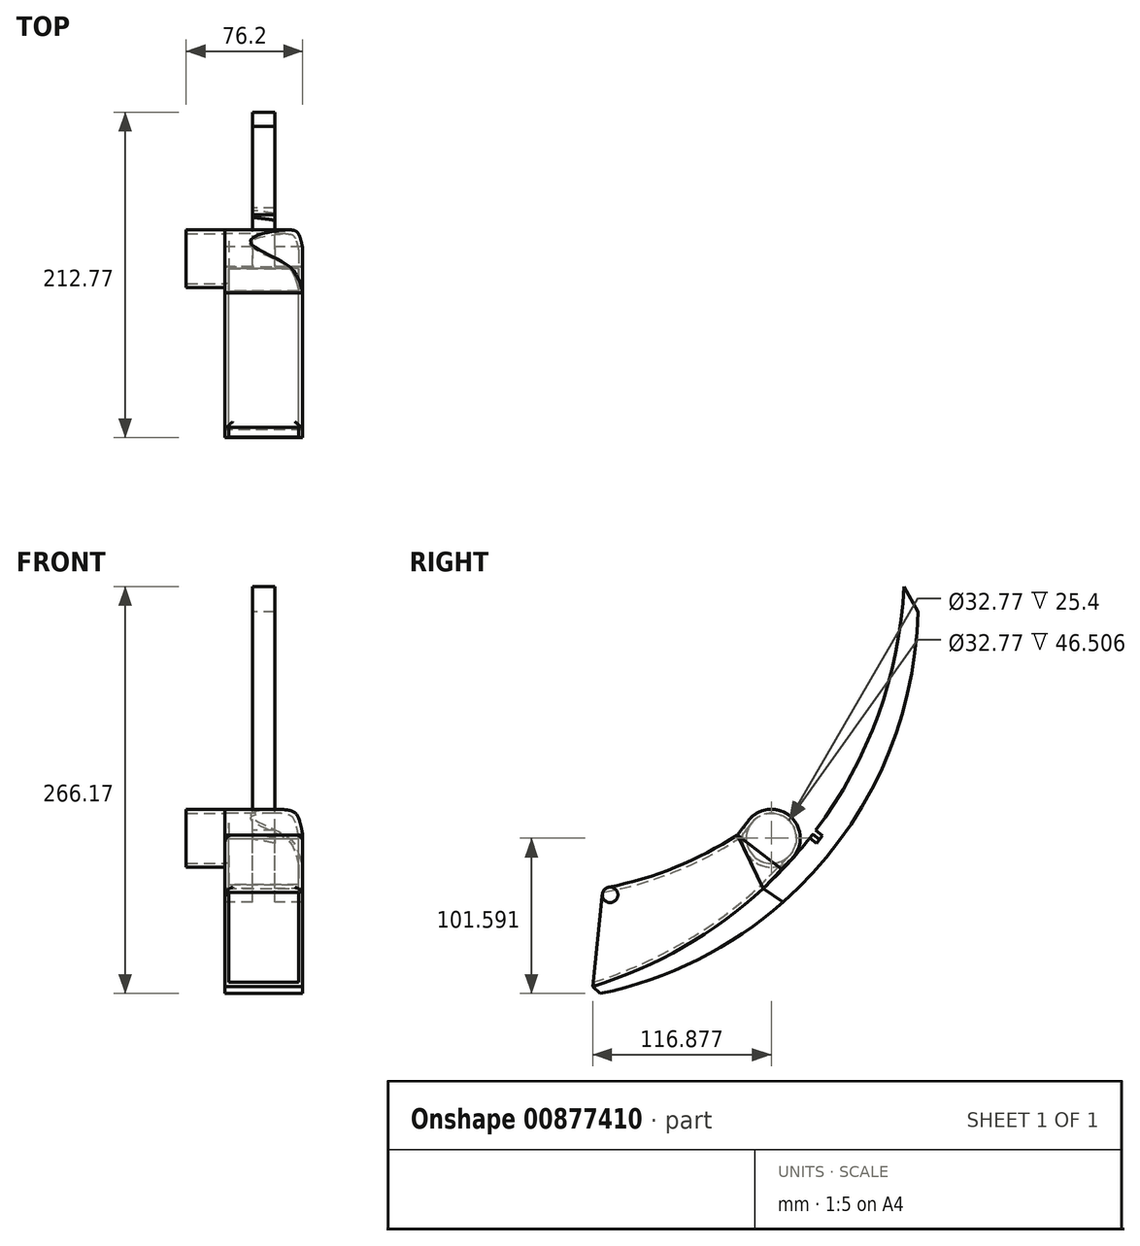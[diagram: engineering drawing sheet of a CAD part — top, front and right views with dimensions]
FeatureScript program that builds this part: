
annotation { "Feature Type Name" : "Feature", "Feature Type Description" : "" }
export const myFeature = defineFeature(function(context is Context, id is Id, definition is map)
    precondition{}
    {
        {
            var Q0;
            Q0=qCreatedBy(makeId("Right.planeOp"),FACE);
            var sketch = newSketch(context, id + "F0", { "sketchPlane" : qUnion([Q0])});
            skLineSegment(sketch, "E0", {"start": v(0, 254) * mm, "end": v(-9.14, 270.4) * mm});
            skLineSegment(sketch, "E1", {"start": v(-212.77, 8.9) * mm, "end": v(-207.84, 4.23) * mm});
            skArc(sketch, "E2", {"start": v(-207.84, 4.23) * mm, "mid": v(-60.3, 92.82) * mm, "end": v(0, 254) * mm});
            skArc(sketch, "E3", {"start": v(-212.77, 8.9) * mm, "mid": v(-69.6, 107.45) * mm, "end": v(-9.14, 270.4) * mm});
            skLineSegment(sketch, "E4", {"start": v(-88.1, 64.18) * mm, "end": v(-101.15, 73.07) * mm});
            skSolve(sketch);
        }
        {
            var Q0;
            Q0=makeQuery(id+"F0.imprint","IMPRINT",FACE,{"disambiguationData":[TD([[makeQuery(id+"F0.imprint","IMPRINT",EDGE,{"derivedFrom":sQuery(id+"F0.wireOp",EDGE,"E0")}),1.0]])]});
            extrude(context, id + "F1", {"entities" : qUnion([Q0]), "endBound" : BoundingType.SYMMETRIC, "depth" : 14.6 * mm, "offsetDistance" : 25.4 * mm});
        }
        {
            var Q0;
            {var subQ0=sQuery(id+"F0.wireOp",EDGE,"E1");Q0=makeQuery(id+"F0.imprint","IMPRINT",FACE,{"disambiguationData":[TD([[makeQuery(id+"F0.imprint","IMPRINT",EDGE,{"derivedFrom":subQ0}),1.0]])]});}
            extrude(context, id + "F2", {"entities" : qUnion([Q0]), "operationType" : NewBodyOperationType.ADD, "endBound" : BoundingType.SYMMETRIC, "depth" : 50.8 * mm, "offsetDistance" : 25.4 * mm});
        }
        {
            var Q0;
            Q0=makeQuery(id+"F2.opExtrude","CAP_FACE",FACE,{"disambiguationData":[OSD([sQuery(id+"F0.wireOp",EDGE,"E1"),sQuery(id+"F0.wireOp",EDGE,"E2"),sQuery(id+"F0.wireOp",EDGE,"E3"),sQuery(id+"F0.wireOp",EDGE,"E4")])],"isStart":false});
            var sketch = newSketch(context, id + "F3", { "sketchPlane" : qUnion([Q0])});
            skLineSegment(sketch, "E5", {"start": v(-101.15, 73.07) * mm, "end": v(-118.1, 107.95) * mm});
            skLineSegment(sketch, "E6", {"start": v(-212.77, 8.9) * mm, "end": v(-206.02, 73.07) * mm});
            skArc(sketch, "E7", {"start": v(-206.02, 73.07) * mm, "mid": v(-160.33, 86.16) * mm, "end": v(-118.1, 107.95) * mm});
            skSolve(sketch);
        }
        {
            var Q0;
            Q0=makeQuery(id+"F3.imprint","IMPRINT",FACE,{"disambiguationData":[TD([[makeQuery(id+"F3.imprint","IMPRINT",EDGE,{"derivedFrom":sQuery(id+"F3.wireOp",EDGE,"E5")}),1.0]])]});
            extrude(context, id + "F4", {"entities" : qUnion([Q0]), "oppositeDirection" : true, "depth" : 50.8 * mm, "offsetDistance" : 25.4 * mm});
        }
        {
            var Q0;
            Q0=makeQuery(id+"F4.opExtrude","SWEPT_FACE",FACE,{"disambiguationData":[OSD([sQuery(id+"F3.wireOp",EDGE,"E6")])]});
            var Q1;
            Q1=makeQuery(id+"F4.opExtrude","SWEPT_FACE",FACE,{"disambiguationData":[OSD([sQuery(id+"F3.wireOp",EDGE,"E5")])]});
            shell(context, id + "F5", {"entities" : qUnion([Q0, Q1]), "thickness" : 2.54 * mm});
        }
        {
            var Q0;
            Q0=makeQuery(id+"F4.opExtrude","CAP_FACE",FACE,{"disambiguationData":[OSD([sQuery(id+"F0.wireOp",EDGE,"E3"),sQuery(id+"F3.wireOp",EDGE,"E5"),sQuery(id+"F3.wireOp",EDGE,"E6"),sQuery(id+"F3.wireOp",EDGE,"E7")])],"isStart":false});
            var sketch = newSketch(context, id + "F6", { "sketchPlane" : qUnion([Q0])});
            skCircle(sketch, "E8", {"center": v(95.9, 105.82) * mm, "radius": 18.92 * mm});
            skLineSegment(sketch, "E9", {"start": v(82.26, 92.7) * mm, "end": v(101.15, 73.07) * mm});
            skLineSegment(sketch, "E10", {"start": v(110.92, 117.32) * mm, "end": v(118.1, 107.95) * mm});
            skSolve(sketch);
        }
        {
            var Q0;
            Q0=makeQuery(id+"F6.imprint","IMPRINT",FACE,{"disambiguationData":[TD([[makeQuery(id+"F6.imprint","IMPRINT",EDGE,{"derivedFrom":sQuery(id+"F6.wireOp",EDGE,"E8")}),1.0]])]});
            extrude(context, id + "F7", {"entities" : qUnion([Q0]), "depth" : 25.4 * mm, "offsetDistance" : 25.4 * mm});
        }
        {
            var Q0;
            {var subQ0=sQuery(id+"F6.wireOp",EDGE,"E9");Q0=makeQuery(id+"F6.imprint","IMPRINT",FACE,{"disambiguationData":[TD([[makeQuery(id+"F6.imprint","IMPRINT",EDGE,{"derivedFrom":subQ0}),1.0]])]});}
            var Q1;
            {var subQ0=sQuery(id+"F6.wireOp",EDGE,"E8");var subQ1=makeQuery(id+"F6.imprint","INTERSECT",VERTEX,{"derivedFrom":[subQ0,sQuery(id+"F6.wireOp",EDGE,"E9")]});Q1=makeQuery(id+"F6.imprint","IMPRINT",FACE,{"disambiguationData":[TD([[makeQuery(id+"F6.imprint","IMPRINT",EDGE,{"disambiguationData":[TD([[subQ1,1.0]])],"derivedFrom":subQ0}),1.0]])]});}
            extrude(context, id + "F8", {"entities" : qUnion([Q0, Q1]), "depth" : -50.8 * mm, "offsetDistance" : 25.4 * mm});
        }
        {
            var Q0;
            Q0=makeQuery(id+"F8.opExtrude","SWEPT_FACE",FACE,{"disambiguationData":[OSD([sQuery(id+"F6.wireOp",EDGE,"E10")])]});
            var sketch = newSketch(context, id + "F9", { "sketchPlane" : qUnion([Q0])});
            skLineSegment(sketch, "E11", {"start": v(25.4, 47.4) * mm, "end": v(-25.73, 47.4) * mm});
            skLineSegment(sketch, "E12", {"start": v(25.4, 25.74) * mm, "end": v(25.4, 47.4) * mm});
            skFitSpline(sketch, "E13", {"points": [v(25.4, 13.94) * mm, v(21.9, 30.28) * mm, v(14.62, 38.34) * mm, v(-25.73, 47.4) * mm], "startDerivative": vector(-9.18, 60.7) * mm, "endDerivative": vector(-104.54, 16.19) * mm});
            skSolve(sketch);
        }
        {
            var Q0;
            Q0 = qSketchRegion(id + "F9", true);
            var Q1;
            {var subQ0=sQuery(id+"F9.wireOp",EDGE,"o8rzQVCB-Ok8N-V7Tp-5FZD-O7UHBudSxoyC");Q1=makeQuery(id+"F9.imprint","IMPRINT",FACE,{"disambiguationData":[TD([[makeQuery(id+"F9.imprint","IMPRINT",EDGE,{"derivedFrom":subQ0}),1.0]])]});}
            var Q2;
            {var subQ0=sQuery(id+"F9.wireOp",EDGE,"E11");Q2=makeQuery(id+"F9.imprint","IMPRINT",FACE,{"disambiguationData":[TD([[makeQuery(id+"F9.imprint","IMPRINT",EDGE,{"derivedFrom":subQ0}),1.0]])]});}
            var Q3;
            {var subQ1=sQuery(id+"F6.wireOp",EDGE,"E10");var subQ2=makeQuery(id+"F8.opExtrude","CAP_EDGE",EDGE,{"disambiguationData":[OSD([subQ1])],"isStart":false});Q3=makeQuery(id+"F9.imprint","IMPRINT",FACE,{"disambiguationData":[TD([[makeQuery(id+"F9.imprint","IMPRINT",EDGE,{"derivedFrom":subQ2}),-1.0]])]});}
            extrude(context, id + "F10", {"entities" : qUnion([Q0, Q1, Q2, Q3]), "operationType" : NewBodyOperationType.REMOVE, "oppositeDirection" : true, "depth" : 44.45 * mm, "offsetDistance" : 25.4 * mm});
        }
        {
            var Q0;
            Q0=makeQuery(id+"F7.opExtrude","CAP_FACE",FACE,{"disambiguationData":[OSD([sQuery(id+"F6.wireOp",EDGE,"E8")])],"isStart":false});
            shell(context, id + "F11", {"entities" : qUnion([Q0]), "thickness" : 2.54 * mm});
        }
        {
            var Q0;
            Q0=makeQuery(id+"F8.opExtrude","SWEPT_FACE",FACE,{"disambiguationData":[OSD([sQuery(id+"F3.wireOp",EDGE,"E5")])]});
            shell(context, id + "F12", {"entities" : qUnion([Q0]), "thickness" : 2.54 * mm});
        }
        {
            var Q0;
            Q0=makeQuery(id+"F10.boolean.opBoolean","COPY",EDGE,{"derivedFrom":makeQuery(id+"F10.opExtrude","CAP_EDGE",EDGE,{"disambiguationData":[OSD([sQuery(id+"F9.wireOp",EDGE,"E13")])],"isStart":true})});
            var Q1;
            Q1=makeQuery(id+"F4.opExtrude","CAP_EDGE",EDGE,{"disambiguationData":[OSD([sQuery(id+"F3.wireOp",EDGE,"E7")])],"isStart":true});
            var Q2;
            Q2=makeQuery(id+"F4.opExtrude","CAP_EDGE",EDGE,{"disambiguationData":[OSD([sQuery(id+"F3.wireOp",EDGE,"E7")])],"isStart":false});
            var Q3;
            Q3=makeQuery(id+"F4.opExtrude","SWEPT_EDGE",EDGE,{"disambiguationData":[OSD([sQuery(id+"F3.wireOp",EDGE,"E6"),sQuery(id+"F3.wireOp",EDGE,"E7")])]});
            fillet(context, id + "F13", {"entities" : qUnion([Q0, Q1, Q2, Q3]), "radius" : 5.08 * mm, "tangentPropagation" : true, "allowEdgeOverflow" : false});
        }
        {
            var Q0;
            {var subQ0=sQuery(id+"F6.wireOp",EDGE,"E8");Q0=makeQuery(id+"F11.opShell","OFFSET_FACE",FACE,{"disambiguationData":[OSD([subQ0]),TDD([makeQuery(id+"F7.opExtrude","CAP_FACE",FACE,{"disambiguationData":[OSD([subQ0])],"isStart":true})])]});}
            extrude(context, id + "F14", {"entities" : qUnion([Q0]), "operationType" : NewBodyOperationType.REMOVE, "oppositeDirection" : true, "depth" : 5.08 * mm, "offsetDistance" : 25.4 * mm});
        }
    });
